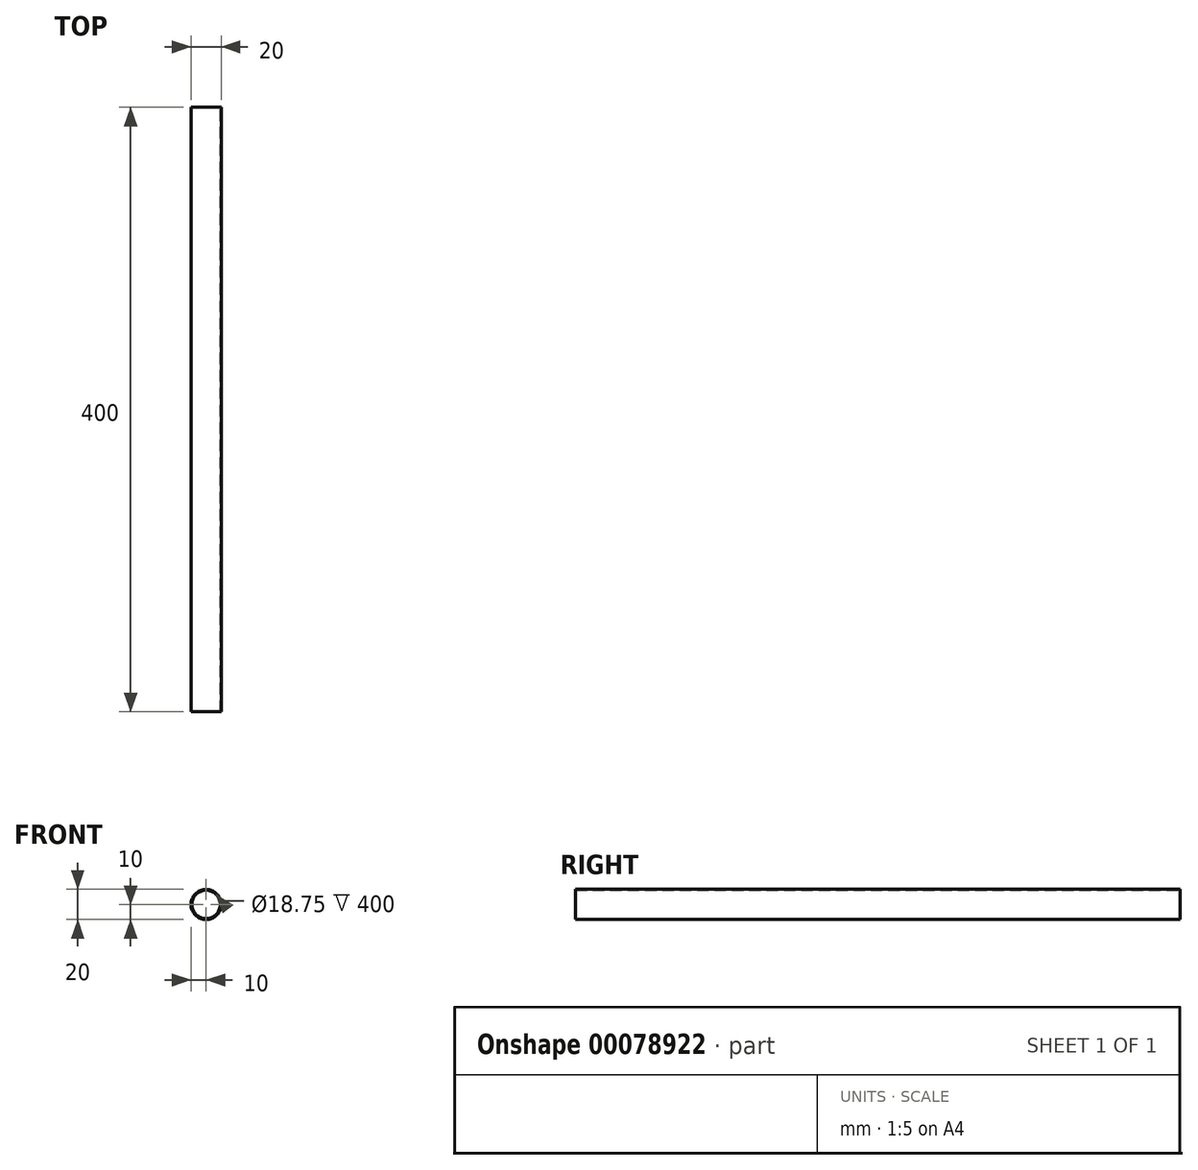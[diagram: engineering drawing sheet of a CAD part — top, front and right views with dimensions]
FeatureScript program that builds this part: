
annotation { "Feature Type Name" : "Feature", "Feature Type Description" : "" }
export const myFeature = defineFeature(function(context is Context, id is Id, definition is map)
    precondition{}
    {
        {
            var Q0;
            Q0=qCreatedBy(makeId("Front.planeOp"),FACE);
            var sketch = newSketch(context, id + "F1", { "sketchPlane" : qUnion([Q0])});
            skCircle(sketch, "E0", {"center": v(0, 0) * mm, "radius": 10 * mm});
            skCircle(sketch, "E1", {"center": v(0, 0) * mm, "radius": 9.38 * mm});
            skSolve(sketch);
        }
        {
            var Q0;
            Q0=qSketchRegion(id+"F1",true);
            extrude(context, id + "F0", {"entities" : qUnion([Q0]), "depth" : 400 * mm});
        }
    });
